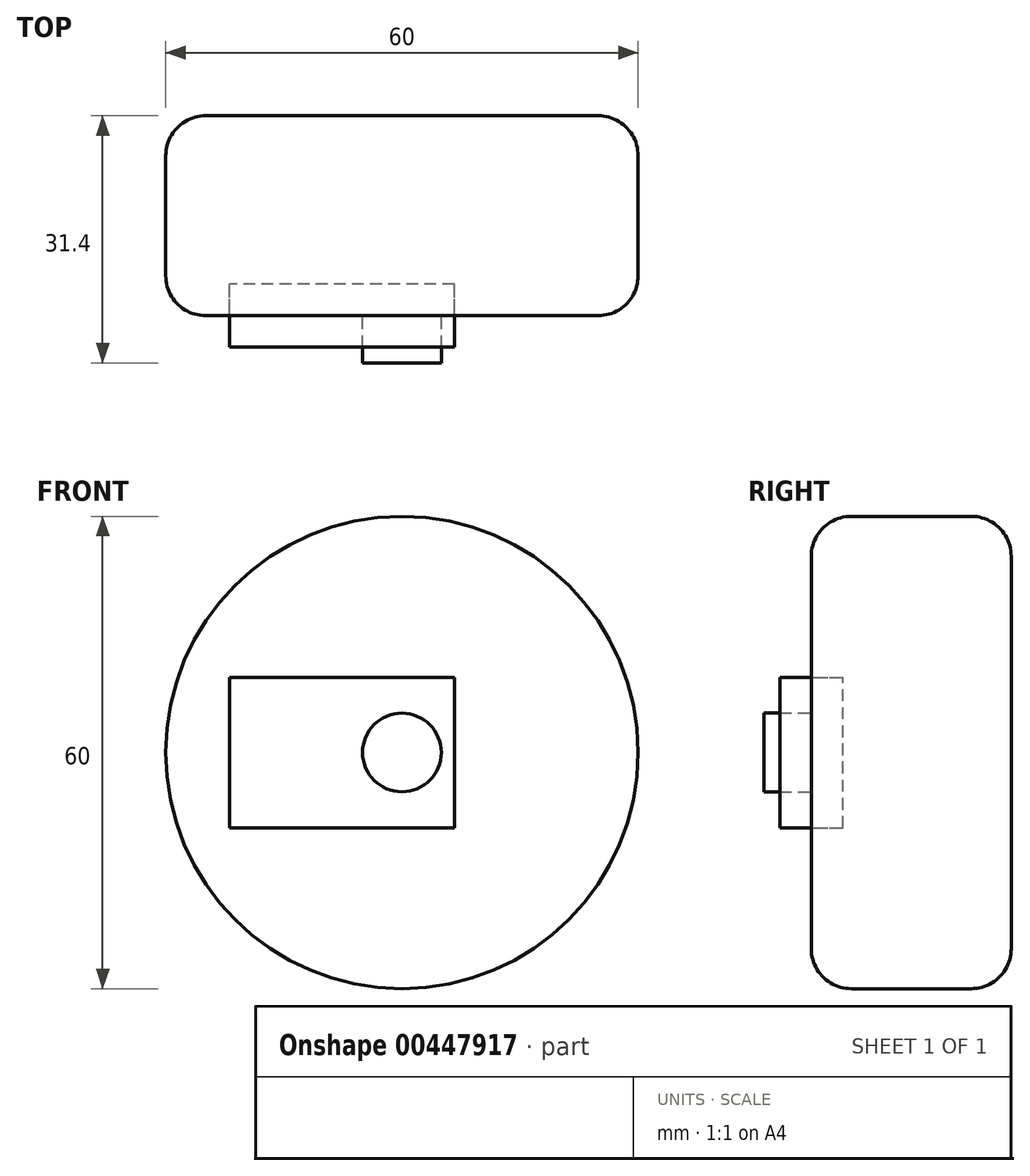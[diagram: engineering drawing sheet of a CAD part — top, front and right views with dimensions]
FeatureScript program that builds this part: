
annotation { "Feature Type Name" : "Feature", "Feature Type Description" : "" }
export const myFeature = defineFeature(function(context is Context, id is Id, definition is map)
    precondition{}
    {
        {
            var Q0;
            Q0=qCreatedBy(makeId("Front.planeOp"),FACE);
            var sketch = newSketch(context, id + "F0", { "sketchPlane" : qUnion([Q0])});
            skCircle(sketch, "E0", {"center": v(0, 0) * mm, "radius": 30 * mm});
            skSolve(sketch);
        }
        {
            var Q0;
            Q0=makeQuery(id+"F0.imprint","IMPRINT",FACE,{"disambiguationData":[TD([[makeQuery(id+"F0.imprint","IMPRINT",EDGE,{"derivedFrom":sQuery(id+"F0.wireOp",EDGE,"E0")}),1.0]])]});
            extrude(context, id + "F1", {"entities" : qUnion([Q0]), "depth" : 25.4 * mm});
        }
        {
            var Q0;
            Q0=makeQuery(id+"F1.opExtrude","CAP_EDGE",EDGE,{"disambiguationData":[OSD([sQuery(id+"F0.wireOp",EDGE,"E0")])],"isStart":false});
            var Q1;
            Q1=makeQuery(id+"F1.opExtrude","CAP_EDGE",EDGE,{"disambiguationData":[OSD([sQuery(id+"F0.wireOp",EDGE,"E0")])],"isStart":true});
            var Q2;
            Q2=makeQuery(id+"F1.opExtrude","CAP_FACE",FACE,{"disambiguationData":[OSD([sQuery(id+"F0.wireOp",EDGE,"E0")])],"isStart":false});
            fillet(context, id + "F2", {"entities" : qUnion([Q0, Q1, Q2]), "radius" : 5.08 * mm, "tangentPropagation" : true, "allowEdgeOverflow" : false});
        }
        {
            var Q0;
            Q0=makeQuery(id+"F1.opExtrude","CAP_FACE",FACE,{"disambiguationData":[OSD([sQuery(id+"F0.wireOp",EDGE,"E0")])],"isStart":false});
            var sketch = newSketch(context, id + "F3", { "sketchPlane" : qUnion([Q0])});
            skCircle(sketch, "E1", {"center": v(0, 0) * mm, "radius": 5 * mm});
            skSolve(sketch);
        }
        {
            var Q0;
            Q0=makeQuery(id+"F3.imprint","IMPRINT",FACE,{"disambiguationData":[TD([[makeQuery(id+"F3.imprint","IMPRINT",EDGE,{"derivedFrom":sQuery(id+"F3.wireOp",EDGE,"E1")}),-1.0]])]});
            var Q1;
            Q1=makeQuery(id+"F3.imprint","IMPRINT",FACE,{"disambiguationData":[TD([[makeQuery(id+"F3.imprint","IMPRINT",EDGE,{"derivedFrom":sQuery(id+"F3.wireOp",EDGE,"E1")}),1.0]])]});
            extrude(context, id + "F4", {"entities" : qUnion([Q0, Q1]), "operationType" : NewBodyOperationType.ADD, "oppositeDirection" : true, "depth" : 25.4 * mm});
        }
        {
            var Q0;
            Q0=makeQuery(id+"F1.opExtrude","CAP_FACE",FACE,{"disambiguationData":[OSD([sQuery(id+"F0.wireOp",EDGE,"E0")])],"isStart":false});
            var sketch = newSketch(context, id + "F5", { "sketchPlane" : qUnion([Q0])});
            skSolve(sketch);
        }
        {
            var Q0;
            {var subQ0=sQuery(id+"F0.wireOp",EDGE,"E0");Q0=makeQuery(id+"F5.imprint","IMPRINT",FACE,{"disambiguationData":[TD([[makeQuery(id+"F5.imprint","IMPRINT",EDGE,{"derivedFrom":makeQuery(id+"F2.opFillet","BLEND_EDGE",EDGE,{"blendedFrom":[makeQuery(id+"F1.opExtrude","CAP_EDGE",EDGE,{"disambiguationData":[OSD([subQ0])],"isStart":false}),makeQuery(id+"F1.opExtrude","CAP_FACE",FACE,{"disambiguationData":[OSD([subQ0])],"isStart":false})],"blendedInto":[makeQuery(id+"F1.opExtrude","CAP_FACE",FACE,{"disambiguationData":[OSD([subQ0])],"isStart":false})]})}),1.0]])]});}
            var sketch = newSketch(context, id + "F6", { "sketchPlane" : qUnion([Q0])});
            skCircle(sketch, "E2", {"center": v(0, 0) * mm, "radius": 5 * mm});
            skSolve(sketch);
        }
        {
            var Q0;
            Q0=makeQuery(id+"F6.imprint","IMPRINT",FACE,{"disambiguationData":[TD([[makeQuery(id+"F6.imprint","IMPRINT",EDGE,{"derivedFrom":sQuery(id+"F6.wireOp",EDGE,"E2")}),1.0]])]});
            extrude(context, id + "F7", {"entities" : qUnion([Q0]), "operationType" : NewBodyOperationType.ADD, "depth" : 6 * mm});
        }
        {
            var Q0;
            {var subQ0=sQuery(id+"F0.wireOp",EDGE,"E0");Q0=makeQuery(id+"F5.imprint","IMPRINT",FACE,{"disambiguationData":[TD([[makeQuery(id+"F5.imprint","IMPRINT",EDGE,{"derivedFrom":makeQuery(id+"F2.opFillet","BLEND_EDGE",EDGE,{"blendedFrom":[makeQuery(id+"F1.opExtrude","CAP_EDGE",EDGE,{"disambiguationData":[OSD([subQ0])],"isStart":false}),makeQuery(id+"F1.opExtrude","CAP_FACE",FACE,{"disambiguationData":[OSD([subQ0])],"isStart":false})],"blendedInto":[makeQuery(id+"F1.opExtrude","CAP_FACE",FACE,{"disambiguationData":[OSD([subQ0])],"isStart":false})]})}),1.0]])]});}
            var sketch = newSketch(context, id + "F8", { "sketchPlane" : qUnion([Q0])});
            skLineSegment(sketch, "E3.bottom", {"start": v(6.66, -9.56) * mm, "end": v(-21.9, -9.56) * mm});
            skLineSegment(sketch, "E3.top", {"start": v(6.66, 9.56) * mm, "end": v(-21.9, 9.56) * mm});
            skLineSegment(sketch, "E3.left", {"start": v(6.66, -9.56) * mm, "end": v(6.66, 9.56) * mm});
            skLineSegment(sketch, "E3.right", {"start": v(-21.9, -9.56) * mm, "end": v(-21.9, 9.56) * mm});
            skPoint(sketch, "E3.middle", {"position": v(-7.63, 0) * mm});
            skSolve(sketch);
        }
        {
            var Q0;
            Q0=makeQuery(id+"F8.imprint","IMPRINT",FACE,{"disambiguationData":[TD([[makeQuery(id+"F8.imprint","IMPRINT",EDGE,{"derivedFrom":sQuery(id+"F8.wireOp",EDGE,"E3.bottom")}),-1.0]])]});
            extrude(context, id + "F9", {"entities" : qUnion([Q0]), "endBound" : BoundingType.SYMMETRIC, "depth" : 8 * mm});
        }
    });
